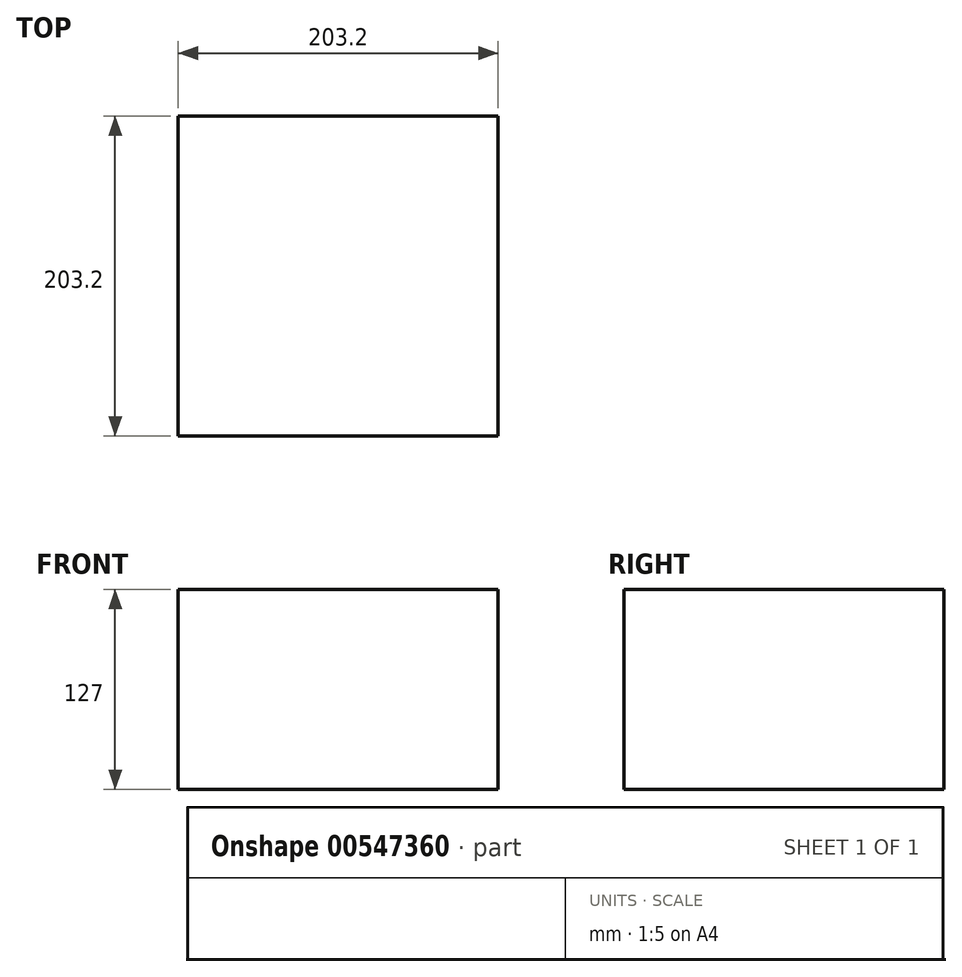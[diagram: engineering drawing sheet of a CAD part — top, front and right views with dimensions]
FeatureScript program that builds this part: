
annotation { "Feature Type Name" : "Feature", "Feature Type Description" : "" }
export const myFeature = defineFeature(function(context is Context, id is Id, definition is map)
    precondition{}
    {
        {
            var Q0;
            Q0=qCreatedBy(makeId("Top.planeOp"),FACE);
            var sketch = newSketch(context, id + "F0", { "sketchPlane" : qUnion([Q0])});
            skLineSegment(sketch, "E0.bottom", {"start": v(101.6, 101.6) * mm, "end": v(-101.6, 101.6) * mm});
            skLineSegment(sketch, "E0.top", {"start": v(101.6, -101.6) * mm, "end": v(-101.6, -101.6) * mm});
            skLineSegment(sketch, "E0.left", {"start": v(101.6, 101.6) * mm, "end": v(101.6, -101.6) * mm});
            skLineSegment(sketch, "E0.right", {"start": v(-101.6, 101.6) * mm, "end": v(-101.6, -101.6) * mm});
            skPoint(sketch, "E0.middle", {"position": v(0, 0) * mm});
            skSolve(sketch);
        }
        {
            var Q0;
            Q0 = qSketchRegion(id + "F0", true);
            extrude(context, id + "F1", {"entities" : qUnion([Q0]), "depth" : 127 * mm, "offsetDistance" : 25.4 * mm});
        }
    });
